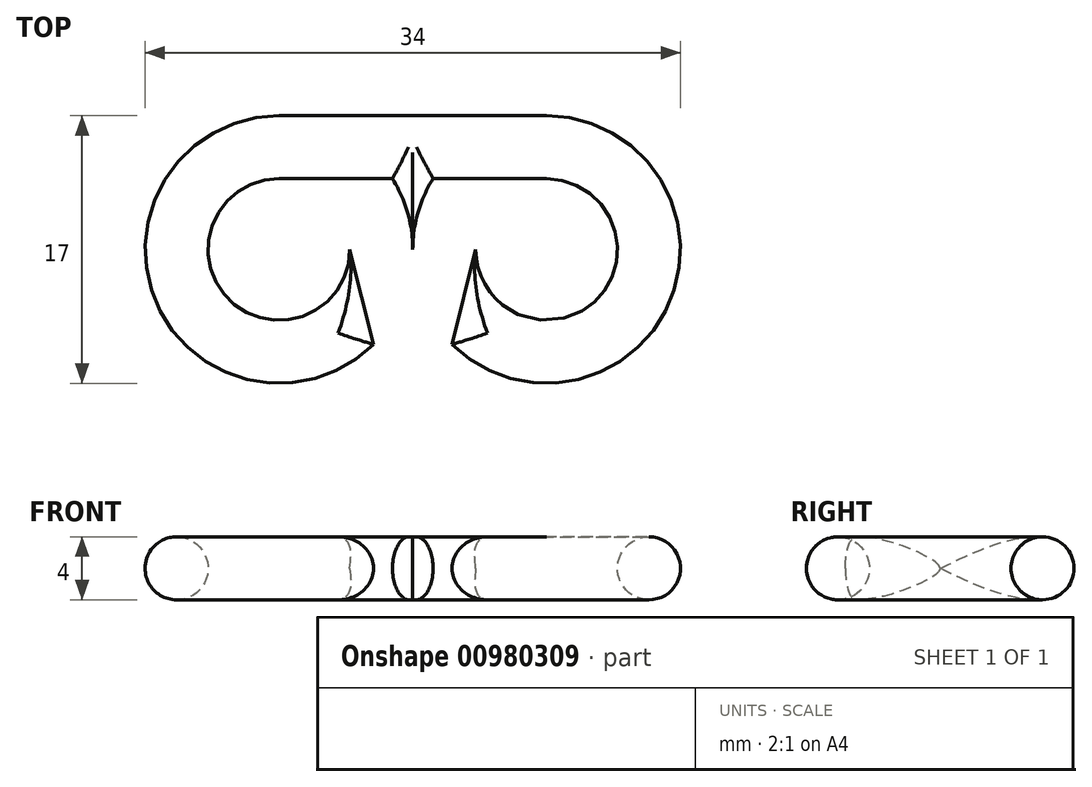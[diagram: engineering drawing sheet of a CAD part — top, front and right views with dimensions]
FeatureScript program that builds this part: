
annotation { "Feature Type Name" : "Feature", "Feature Type Description" : "" }
export const myFeature = defineFeature(function(context is Context, id is Id, definition is map)
    precondition{}
    {
        {
            var Q0;
            Q0=qCreatedBy(makeId("Top.planeOp"),FACE);
            var sketch = newSketch(context, id + "F0", { "sketchPlane" : qUnion([Q0])});
            skArc(sketch, "E0", {"start": v(7.21, 4.5) * mm, "mid": v(-8.44, 0.97) * mm, "end": v(6, -6.02) * mm});
            skArc(sketch, "E1", {"start": v(0, 4.5) * mm, "mid": v(-3.18, -3.18) * mm, "end": v(4.5, 0) * mm});
            skLineSegment(sketch, "E2", {"start": v(0, 8.5) * mm, "end": v(8.5, 8.5) * mm});
            skLineSegment(sketch, "E3", {"start": v(4.5, 0) * mm, "end": v(6, -6.02) * mm});
            skLineSegment(sketch, "E4", {"start": v(0, 4.5) * mm, "end": v(8.5, 4.5) * mm});
            skLineSegment(sketch, "E5", {"start": v(8.5, 4.5) * mm, "end": v(8.5, 8.5) * mm});
            skLineSegment(sketch, "E6.MirrorCS", {"start": v(17, 4.5) * mm, "end": v(8.5, 4.5) * mm});
            skLineSegment(sketch, "E7.MirrorCS", {"start": v(17, 8.5) * mm, "end": v(8.5, 8.5) * mm});
            skArc(sketch, "E8.MirrorCS", {"start": v(9.79, 4.5) * mm, "mid": v(25.44, 0.97) * mm, "end": v(11, -6.02) * mm});
            skArc(sketch, "E9.MirrorCS", {"start": v(17, 4.5) * mm, "mid": v(20.18, -3.18) * mm, "end": v(12.5, 0) * mm});
            skLineSegment(sketch, "E10.MirrorCS", {"start": v(12.5, 0) * mm, "end": v(11, -6.02) * mm});
            skArc(sketch, "E11", {"start": v(7.21, 4.5) * mm, "mid": v(8.17, 2.34) * mm, "end": v(8.5, 0) * mm});
            skArc(sketch, "E12", {"start": v(9.79, 4.5) * mm, "mid": v(8.83, 2.34) * mm, "end": v(8.5, 0) * mm});
            skSolve(sketch);
        }
        {
            var Q0;
            Q0 = qSketchRegion(id + "F0", true);
            var Q1;
            {var subQ1=sQuery(id+"F0.wireOp",EDGE,"E1");Q1=makeQuery(id+"F0.imprint","IMPRINT",FACE,{"disambiguationData":[TD([[makeQuery(id+"F0.imprint","IMPRINT",EDGE,{"derivedFrom":subQ1}),-1.0]])]});}
            extrude(context, id + "F1", {"entities" : qUnion([Q0, Q1]), "depth" : 4 * mm, "offsetDistance" : 25 * mm});
        }
        {
            var Q0;
            Q0=makeQuery(id+"F1.opExtrude","CAP_FACE",FACE,{"disambiguationData":[OSD([sQuery(id+"F0.wireOp",EDGE,"E0"),sQuery(id+"F0.wireOp",EDGE,"E1"),sQuery(id+"F0.wireOp",EDGE,"E2"),sQuery(id+"F0.wireOp",EDGE,"E3"),sQuery(id+"F0.wireOp",EDGE,"E4"),sQuery(id+"F0.wireOp",EDGE,"E6.MirrorCS"),sQuery(id+"F0.wireOp",EDGE,"E7.MirrorCS"),sQuery(id+"F0.wireOp",EDGE,"E8.MirrorCS"),sQuery(id+"F0.wireOp",EDGE,"E9.MirrorCS"),sQuery(id+"F0.wireOp",EDGE,"E10.MirrorCS")])],"isStart":false});
            var Q1;
            Q1=makeQuery(id+"F1.opExtrude","CAP_FACE",FACE,{"disambiguationData":[OSD([sQuery(id+"F0.wireOp",EDGE,"E0"),sQuery(id+"F0.wireOp",EDGE,"E1"),sQuery(id+"F0.wireOp",EDGE,"E2"),sQuery(id+"F0.wireOp",EDGE,"E3"),sQuery(id+"F0.wireOp",EDGE,"E4"),sQuery(id+"F0.wireOp",EDGE,"E6.MirrorCS"),sQuery(id+"F0.wireOp",EDGE,"E7.MirrorCS"),sQuery(id+"F0.wireOp",EDGE,"E8.MirrorCS"),sQuery(id+"F0.wireOp",EDGE,"E9.MirrorCS"),sQuery(id+"F0.wireOp",EDGE,"E10.MirrorCS")])],"isStart":true});
            fillet(context, id + "F2", {"entities" : qUnion([Q0, Q1]), "radius" : 2 * mm, "tangentPropagation" : true, "allowEdgeOverflow" : false});
        }
    });
